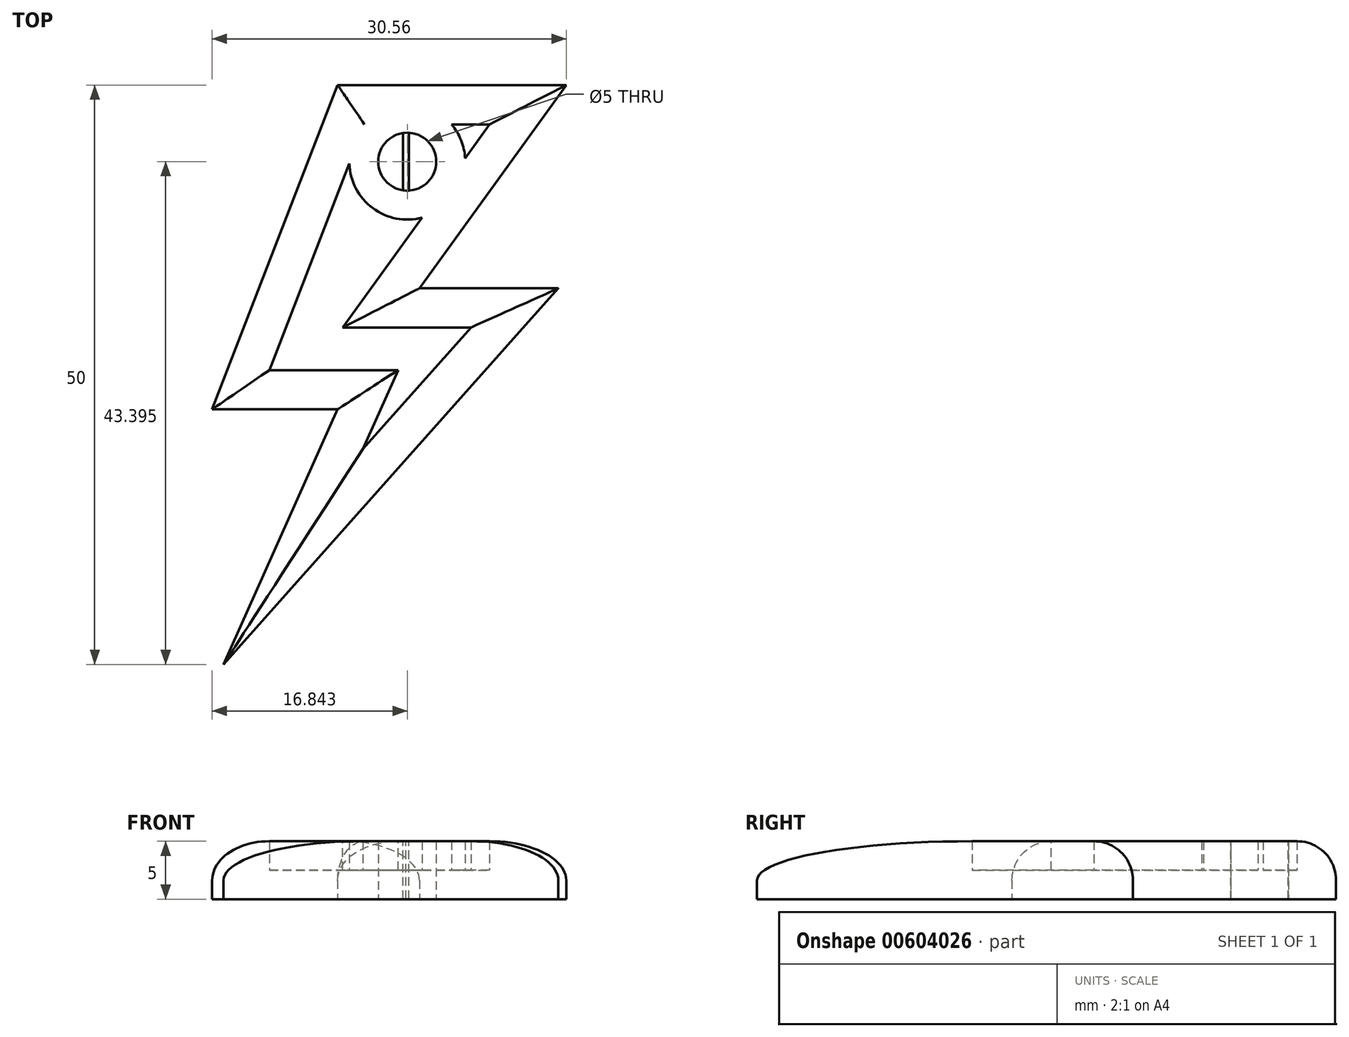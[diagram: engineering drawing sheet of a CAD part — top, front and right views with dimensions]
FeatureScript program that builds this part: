
annotation { "Feature Type Name" : "Feature", "Feature Type Description" : "" }
export const myFeature = defineFeature(function(context is Context, id is Id, definition is map)
    precondition{}
    {
        {
            var Q0;
            Q0=qCreatedBy(makeId("Top.planeOp"),FACE);
            var sketch = newSketch(context, id + "F0", { "sketchPlane" : qUnion([Q0])});
            skLineSegment(sketch, "E0", {"start": v(10.57, -27.85) * mm, "end": v(20.44, -5.83) * mm});
            skLineSegment(sketch, "E1", {"start": v(20.44, -5.83) * mm, "end": v(9.6, -5.83) * mm});
            skLineSegment(sketch, "E2", {"start": v(9.6, -5.83) * mm, "end": v(20.44, 22.15) * mm});
            skLineSegment(sketch, "E3", {"start": v(20.44, 22.15) * mm, "end": v(40.16, 22.15) * mm});
            skLineSegment(sketch, "E4", {"start": v(40.16, 22.15) * mm, "end": v(27.5, 4.62) * mm});
            skLineSegment(sketch, "E5", {"start": v(27.5, 4.62) * mm, "end": v(39.49, 4.62) * mm});
            skLineSegment(sketch, "E6", {"start": v(39.49, 4.62) * mm, "end": v(10.57, -27.85) * mm});
            skSolve(sketch);
        }
        {
            var Q0;
            Q0=makeQuery(id+"F0.imprint","IMPRINT",FACE,{"disambiguationData":[TD([[makeQuery(id+"F0.imprint","IMPRINT",EDGE,{"derivedFrom":sQuery(id+"F0.wireOp",EDGE,"E0")}),-1.0]])]});
            extrude(context, id + "F1", {"entities" : qUnion([Q0]), "depth" : 5 * mm, "offsetDistance" : 25 * mm});
        }
        {
            var Q0;
            Q0=makeQuery(id+"F1.opExtrude","CAP_FACE",FACE,{"disambiguationData":[OSD([sQuery(id+"F0.wireOp",EDGE,"E0"),sQuery(id+"F0.wireOp",EDGE,"E1"),sQuery(id+"F0.wireOp",EDGE,"E2"),sQuery(id+"F0.wireOp",EDGE,"E3"),sQuery(id+"F0.wireOp",EDGE,"E4"),sQuery(id+"F0.wireOp",EDGE,"E5"),sQuery(id+"F0.wireOp",EDGE,"E6")])],"isStart":false});
            var Q1;
            Q1=makeQuery(id+"F1.opExtrude","CAP_EDGE",EDGE,{"disambiguationData":[OSD([sQuery(id+"F0.wireOp",EDGE,"E1")])],"isStart":false});
            fillet(context, id + "F2", {"entities" : qUnion([Q0, Q1]), "radius" : 3.38 * mm, "tangentPropagation" : true, "allowEdgeOverflow" : false});
        }
        {
            var Q0;
            Q0=qCreatedBy(makeId("Top.planeOp"),FACE);
            var sketch = newSketch(context, id + "F3", { "sketchPlane" : qUnion([Q0])});
            skCircle(sketch, "E7", {"center": v(26.44, 15.55) * mm, "radius": 2.6 * mm});
            skSolve(sketch);
        }
        {
            var Q0;
            Q0=sQuery(id+"F3.wireOp",VERTEX,"E7.center");
            var Q1;
            Q1=makeQuery(id+"F1.opExtrude","SWEPT_BODY",BODY,{"disambiguationData":[OSD([sQuery(id+"F0.wireOp",EDGE,"E0"),sQuery(id+"F0.wireOp",EDGE,"E1"),sQuery(id+"F0.wireOp",EDGE,"E2"),sQuery(id+"F0.wireOp",EDGE,"E3"),sQuery(id+"F0.wireOp",EDGE,"E4"),sQuery(id+"F0.wireOp",EDGE,"E5"),sQuery(id+"F0.wireOp",EDGE,"E6")])]});
            hole(context, id + "F4", {"style" : HoleStyle.SIMPLE, "endStyle" : HoleEndStyle.THROUGH, "oppositeDirection" : true, "holeDiameter" : 5 * mm, "majorDiameter" : 5 * mm, "isTappedThrough" : true, "tappedDepth" : 12 * mm, "tapClearance" : 3, "locations" : qUnion([Q0]), "scope" : qUnion([Q1])});
        }
        {
            var Q0;
            Q0=makeQuery(id+"F1.opExtrude","CAP_FACE",FACE,{"disambiguationData":[OSD([sQuery(id+"F0.wireOp",EDGE,"E0"),sQuery(id+"F0.wireOp",EDGE,"E1"),sQuery(id+"F0.wireOp",EDGE,"E2"),sQuery(id+"F0.wireOp",EDGE,"E3"),sQuery(id+"F0.wireOp",EDGE,"E4"),sQuery(id+"F0.wireOp",EDGE,"E5"),sQuery(id+"F0.wireOp",EDGE,"E6")])],"isStart":false});
            var sketch = newSketch(context, id + "F5", { "sketchPlane" : qUnion([Q0])});
            skLineSegment(sketch, "E8", {"start": v(26.06, 18.02) * mm, "end": v(26.06, 17.16) * mm});
            skLineSegment(sketch, "E9", {"start": v(26.06, 17.16) * mm, "end": v(26.06, 13.07) * mm});
            skLineSegment(sketch, "E10", {"start": v(26.06, 13.07) * mm, "end": v(26.31, 13.05) * mm});
            skLineSegment(sketch, "E11", {"start": v(26.31, 13.05) * mm, "end": v(26.57, 13.05) * mm});
            skLineSegment(sketch, "E12", {"start": v(26.57, 13.05) * mm, "end": v(26.57, 18.04) * mm});
            skLineSegment(sketch, "E13", {"start": v(26.06, 18.02) * mm, "end": v(26.57, 18.04) * mm});
            skSolve(sketch);
        }
        {
            var Q0;
            Q0=makeQuery(id+"F5.imprint","IMPRINT",FACE,{"disambiguationData":[TD([[makeQuery(id+"F5.imprint","IMPRINT",EDGE,{"derivedFrom":sQuery(id+"F5.wireOp",EDGE,"E8")}),1.0]])]});
            extrude(context, id + "F6", {"entities" : qUnion([Q0]), "oppositeDirection" : true, "depth" : 5 * mm, "offsetDistance" : 25 * mm});
        }
        {
            var Q0;
            Q0=makeQuery(id+"F1.opExtrude","CAP_FACE",FACE,{"disambiguationData":[OSD([sQuery(id+"F0.wireOp",EDGE,"E0"),sQuery(id+"F0.wireOp",EDGE,"E1"),sQuery(id+"F0.wireOp",EDGE,"E2"),sQuery(id+"F0.wireOp",EDGE,"E3"),sQuery(id+"F0.wireOp",EDGE,"E4"),sQuery(id+"F0.wireOp",EDGE,"E5"),sQuery(id+"F0.wireOp",EDGE,"E6")])],"isStart":false});
            shell(context, id + "F7", {"entities" : qUnion([Q0]), "thickness" : 2.5 * mm});
        }
    });
